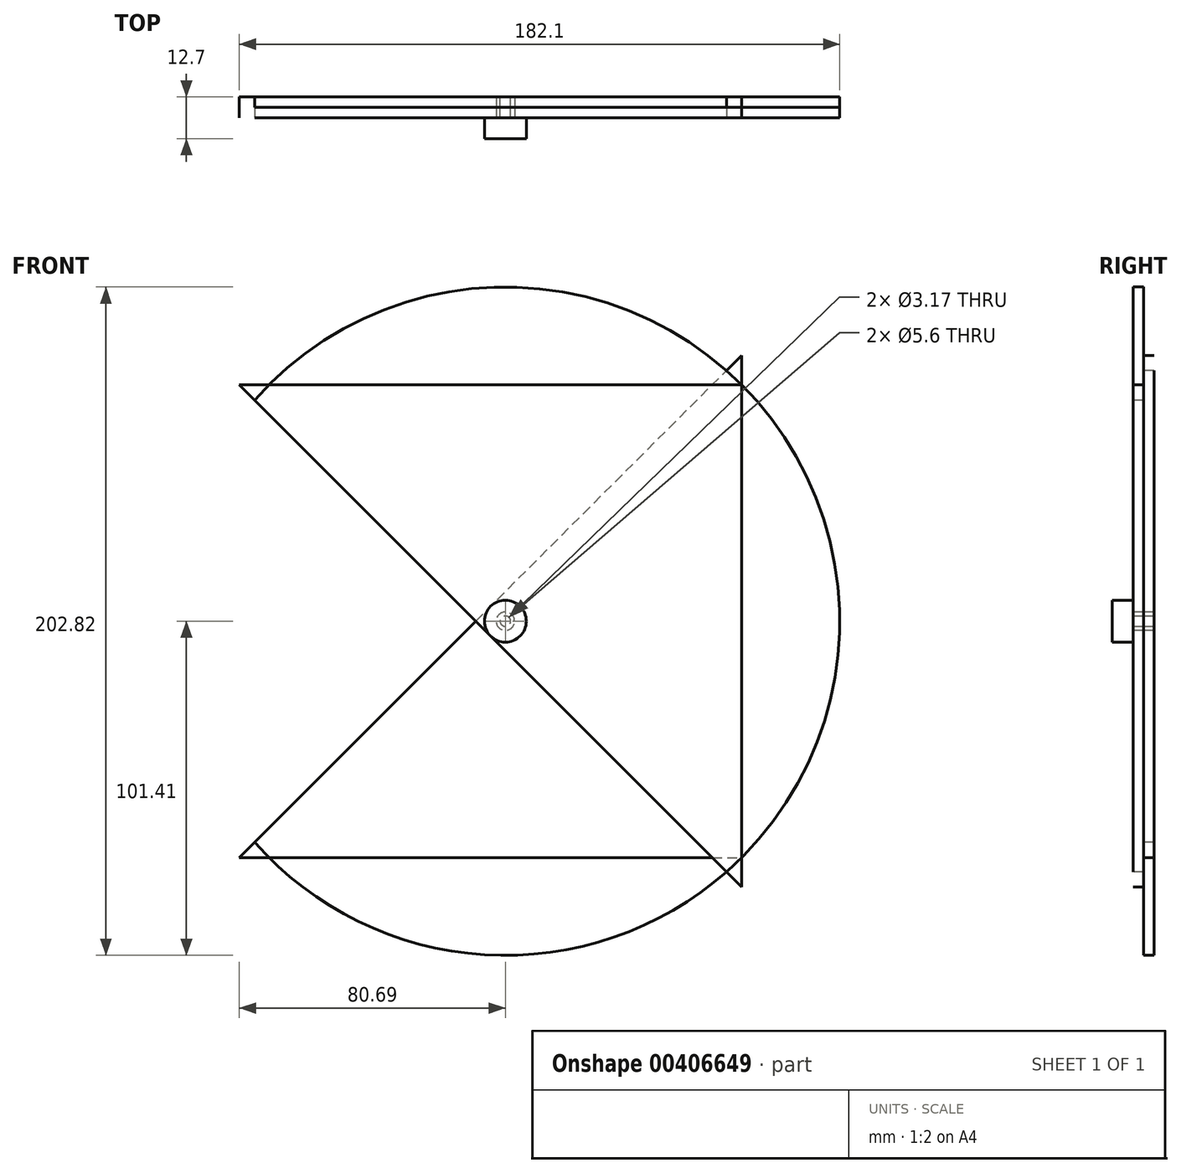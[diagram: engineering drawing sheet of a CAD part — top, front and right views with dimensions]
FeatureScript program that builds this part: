
annotation { "Feature Type Name" : "Feature", "Feature Type Description" : "" }
export const myFeature = defineFeature(function(context is Context, id is Id, definition is map)
    precondition{}
    {
        {
            var Q0;
            Q0=qCreatedBy(makeId("Front.planeOp"),FACE);
            var sketch = newSketch(context, id + "F0", { "sketchPlane" : qUnion([Q0])});
            skLineSegment(sketch, "E0.bottom", {"start": v(-76.2, 76.2) * mm, "end": v(76.2, 76.2) * mm, "construction": true});
            skLineSegment(sketch, "E0.top", {"start": v(-76.2, -76.2) * mm, "end": v(76.2, -76.2) * mm});
            skLineSegment(sketch, "E0.left", {"start": v(-76.2, 76.2) * mm, "end": v(-76.2, -76.2) * mm, "construction": true});
            skLineSegment(sketch, "E0.right", {"start": v(76.2, 76.2) * mm, "end": v(76.2, -76.2) * mm});
            skPoint(sketch, "E0.middle", {"position": v(0, 0) * mm});
            skLineSegment(sketch, "E1", {"start": v(-76.2, -76.2) * mm, "end": v(76.2, 76.2) * mm});
            skLineSegment(sketch, "E2", {"start": v(-76.2, 76.2) * mm, "end": v(76.2, -76.2) * mm, "construction": true});
            skCircle(sketch, "E3", {"center": v(4.5, -4.5) * mm, "radius": 6.35 * mm, "construction": true});
            skCircle(sketch, "E4", {"center": v(4.5, -4.5) * mm, "radius": 1.59 * mm});
            skSolve(sketch);
        }
        {
            var Q0;
            Q0=qSketchRegion(id+"F0",true);
            var Q1;
            Q1=sQuery(id+"F0.wireOp",EDGE,"E0.bottom");
            var Q2;
            Q2=sQuery(id+"F0.wireOp",EDGE,"E0.left");
            extrude(context, id + "F1", {"entities" : qUnion([Q0]), "surfaceEntities" : qUnion([Q1, Q2]), "depth" : 3.17 * mm});
        }
        {
            var Q0;
            Q0=sQuery(id+"F0.wireOp",VERTEX,"E4.center");
            var Q1;
            Q1=qCreatedBy(makeId("Top.planeOp"),FACE);
            cPlane(context, id + "F2", {"entities" : qUnion([Q0, Q1]), "cplaneType" : CPlaneType.PLANE_POINT, "offset" : 25.4 * mm, "width" : 152.4 * mm, "height" : 152.4 * mm});
        }
        {
            var Q0;
            Q0=qCreatedBy(id+"F2.planeOp",FACE);
            var sketch = newSketch(context, id + "F3", { "sketchPlane" : qUnion([Q0])});
            skPoint(sketch, "E5.0", {"position": v(4.5, 0) * mm});
            skLineSegment(sketch, "E6", {"start": v(4.5, 0) * mm, "end": v(4.5, -119.12) * mm});
            skSolve(sketch);
        }
        {
            var Q0;
            Q0=makeQuery(id+"F1.opExtrude","SWEPT_BODY",BODY,{"disambiguationData":[OSD([sQuery(id+"F0.wireOp",EDGE,"E0.top"),sQuery(id+"F0.wireOp",EDGE,"E0.right"),sQuery(id+"F0.wireOp",EDGE,"E1"),sQuery(id+"F0.wireOp",EDGE,"E4")])]});
            var Q1;
            Q1=sQuery(id+"F3.wireOp",EDGE,"E6");
            var Q2;
            Q2=sQuery(id+"F3.wireOp",EDGE,"E6");
            transform(context, id + "F4", {"entities" : qUnion([Q0]), "transformType" : TransformType.ROTATION, "transformAxis" : qUnion([Q2]), "angle" : 90 * degree, "makeCopy" : true});
        }
        {
            var Q0;
            Q0=makeQuery(id+"F4.opPattern","COPY",BODY,{"derivedFrom":makeQuery(id+"F1.opExtrude","SWEPT_BODY",BODY,{"disambiguationData":[OSD([sQuery(id+"F0.wireOp",EDGE,"E0.top"),sQuery(id+"F0.wireOp",EDGE,"E0.right"),sQuery(id+"F0.wireOp",EDGE,"E1"),sQuery(id+"F0.wireOp",EDGE,"E4")])]}),"instanceName":"1"});
            var Q1;
            Q1=sQuery(id+"F3.wireOp",EDGE,"E6");
            transform(context, id + "F5", {"entities" : qUnion([Q0]), "transformType" : TransformType.TRANSLATION_DISTANCE, "transformDirection" : qUnion([Q1]), "distance" : 3.17 * mm, "makeCopy" : false});
        }
        {
            var Q0;
            Q0=makeQuery(id+"F4.opPattern","COPY",FACE,{"derivedFrom":makeQuery(id+"F1.opExtrude","CAP_FACE",FACE,{"disambiguationData":[OSD([sQuery(id+"F0.wireOp",EDGE,"E0.top"),sQuery(id+"F0.wireOp",EDGE,"E0.right"),sQuery(id+"F0.wireOp",EDGE,"E1"),sQuery(id+"F0.wireOp",EDGE,"E4")])],"isStart":false}),"instanceName":"1"});
            var sketch = newSketch(context, id + "F6", { "sketchPlane" : qUnion([Q0])});
            skCircle(sketch, "E7.1", {"center": v(4.5, -4.5) * mm, "radius": 6.35 * mm});
            skSolve(sketch);
        }
        {
            var Q0;
            Q0=qSketchRegion(id+"F6",true);
            extrude(context, id + "F7", {"entities" : qUnion([Q0]), "depth" : 6.35 * mm});
        }
        {
            var Q0;
            Q0=makeQuery(id+"F4.opPattern","COPY",FACE,{"derivedFrom":makeQuery(id+"F1.opExtrude","CAP_FACE",FACE,{"disambiguationData":[OSD([sQuery(id+"F0.wireOp",EDGE,"E0.top"),sQuery(id+"F0.wireOp",EDGE,"E0.right"),sQuery(id+"F0.wireOp",EDGE,"E1"),sQuery(id+"F0.wireOp",EDGE,"E4")])],"isStart":false}),"instanceName":"1"});
            var sketch = newSketch(context, id + "F8", { "sketchPlane" : qUnion([Q0])});
            skLineSegment(sketch, "E8.0", {"start": v(71.57, -80.55) * mm, "end": v(-71.57, 62.59) * mm});
            skArc(sketch, "E9", {"start": v(71.57, -80.55) * mm, "mid": v(76.2, 67.22) * mm, "end": v(-71.57, 62.59) * mm});
            skPoint(sketch, "E10.orphan", {"position": v(-76.2, 67.22) * mm});
            skPoint(sketch, "E11.orphan", {"position": v(76.2, -85.18) * mm});
            skCircle(sketch, "E12", {"center": v(4.5, -4.5) * mm, "radius": 2.8 * mm});
            skSolve(sketch);
        }
        {
            var Q0;
            Q0 = qSketchRegion(id + "F8", true);
            extrude(context, id + "F9", {"entities" : qUnion([Q0]), "oppositeDirection" : true, "depth" : 3.17 * mm});
        }
        {
            var Q0;
            Q0=makeQuery(id+"F9.opExtrude","SWEPT_BODY",BODY,{"disambiguationData":[OSD([sQuery(id+"F8.wireOp",EDGE,"E8.0"),sQuery(id+"F8.wireOp",EDGE,"E9"),sQuery(id+"F8.wireOp",EDGE,"E12")])]});
            var Q1;
            Q1=sQuery(id+"F3.wireOp",EDGE,"E6");
            var Q2;
            Q2=sQuery(id+"F3.wireOp",EDGE,"E6");
            transform(context, id + "F10", {"entities" : qUnion([Q0]), "transformType" : TransformType.ROTATION, "transformAxis" : qUnion([Q2]), "angle" : 90 * degree, "oppositeDirection" : true, "makeCopy" : true});
        }
        {
            var Q0;
            Q0=makeQuery(id+"F10.opPattern","COPY",BODY,{"derivedFrom":makeQuery(id+"F9.opExtrude","SWEPT_BODY",BODY,{"disambiguationData":[OSD([sQuery(id+"F8.wireOp",EDGE,"E8.0"),sQuery(id+"F8.wireOp",EDGE,"E9"),sQuery(id+"F8.wireOp",EDGE,"E12")])]}),"instanceName":"1"});
            var Q1;
            Q1=sQuery(id+"F3.wireOp",EDGE,"E6");
            transform(context, id + "F11", {"entities" : qUnion([Q0]), "transformType" : TransformType.TRANSLATION_DISTANCE, "transformDirection" : qUnion([Q1]), "distance" : 3.17 * mm, "oppositeDirection" : true, "makeCopy" : false});
        }
    });
